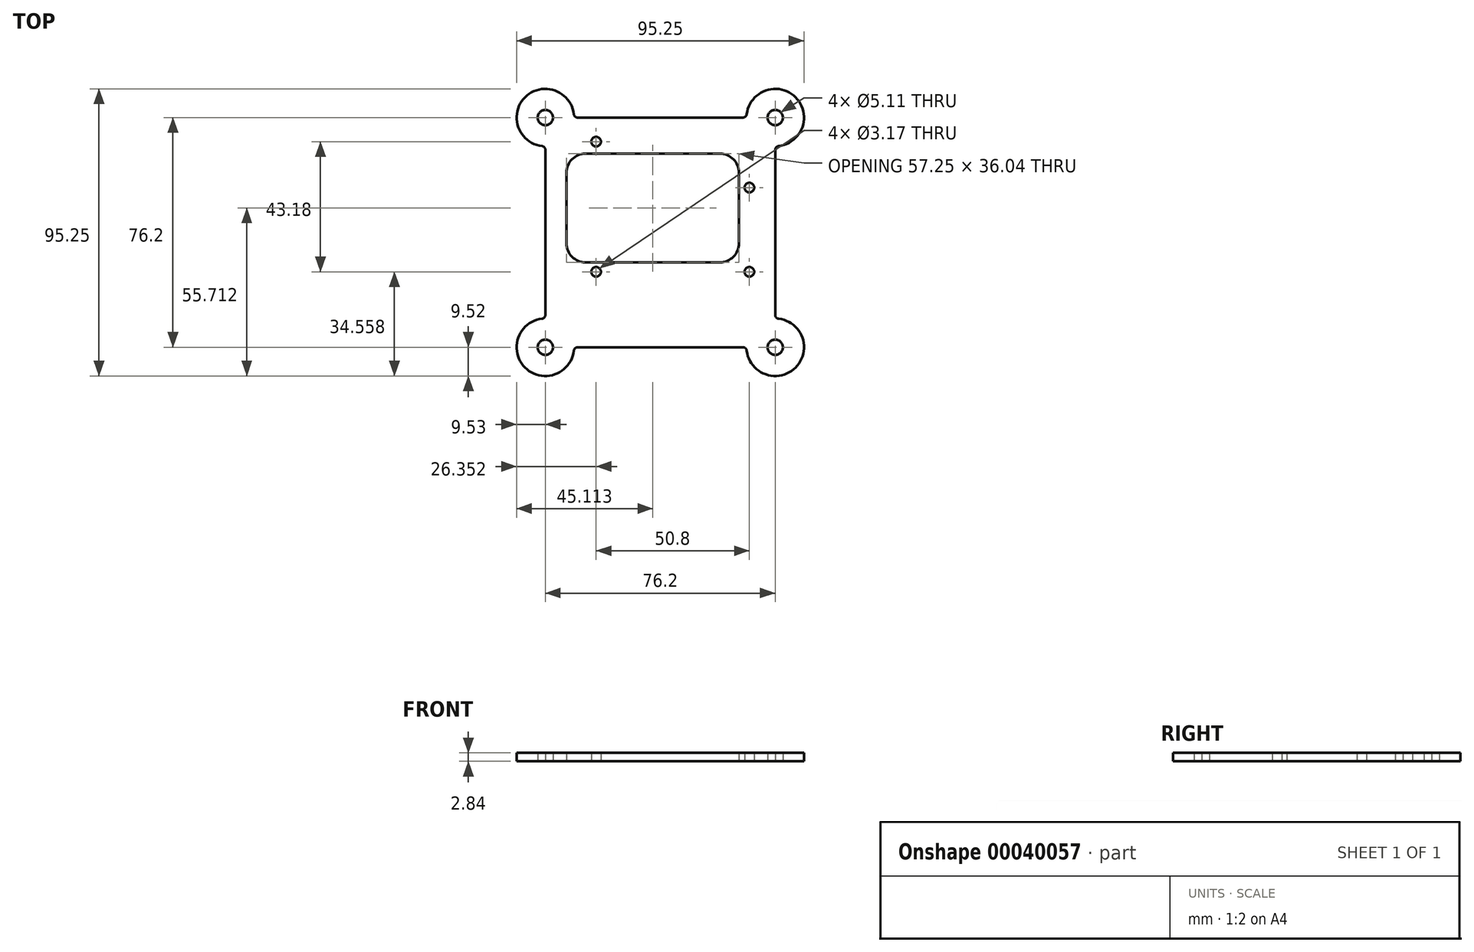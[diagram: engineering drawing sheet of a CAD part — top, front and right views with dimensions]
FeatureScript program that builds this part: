
annotation { "Feature Type Name" : "Feature", "Feature Type Description" : "" }
export const myFeature = defineFeature(function(context is Context, id is Id, definition is map)
    precondition{}
    {
        {
            var Q0;
            Q0=qCreatedBy(makeId("Top.planeOp"),FACE);
            var sketch = newSketch(context, id + "F0", { "sketchPlane" : qUnion([Q0])});
            skCircle(sketch, "E0", {"center": v(-21.62, 22.73) * mm, "radius": 1.59 * mm});
            skCircle(sketch, "E1", {"center": v(29.18, 7.49) * mm, "radius": 1.59 * mm});
            skCircle(sketch, "E2", {"center": v(29.18, -20.45) * mm, "radius": 1.59 * mm});
            skCircle(sketch, "E3", {"center": v(-21.62, -20.45) * mm, "radius": 1.59 * mm});
            skLineSegment(sketch, "E4.bottom", {"start": v(-27.72, 30.71) * mm, "end": v(27.04, 30.71) * mm});
            skLineSegment(sketch, "E4.top", {"start": v(-27.72, -45.49) * mm, "end": v(27.04, -45.49) * mm});
            skLineSegment(sketch, "E4.right", {"start": v(37.76, 20) * mm, "end": v(37.76, -34.77) * mm});
            skArc(sketch, "E5", {"start": v(38.88, 21.25) * mm, "mid": v(44.5, 37.45) * mm, "end": v(28.3, 31.83) * mm});
            skArc(sketch, "E6", {"start": v(28.3, -46.61) * mm, "mid": v(44.5, -52.22) * mm, "end": v(38.88, -36.03) * mm});
            skArc(sketch, "E7", {"start": v(-28.98, 31.83) * mm, "mid": v(-45.18, 37.45) * mm, "end": v(-39.56, 21.25) * mm});
            skArc(sketch, "E8", {"start": v(-39.56, -36.03) * mm, "mid": v(-45.18, -52.22) * mm, "end": v(-28.98, -46.61) * mm});
            skCircle(sketch, "E9", {"center": v(37.76, 30.71) * mm, "radius": 2.55 * mm});
            skCircle(sketch, "E10", {"center": v(-38.44, 30.71) * mm, "radius": 2.55 * mm});
            skCircle(sketch, "E11", {"center": v(-38.44, -45.49) * mm, "radius": 2.55 * mm});
            skCircle(sketch, "E12", {"center": v(37.76, -45.49) * mm, "radius": 2.55 * mm});
            skLineSegment(sketch, "E13.trimOffspring", {"start": v(-38.44, 20) * mm, "end": v(-38.44, -34.77) * mm});
            skLineSegment(sketch, "E14.bottom", {"start": v(-25.13, 18.72) * mm, "end": v(19.42, 18.72) * mm});
            skLineSegment(sketch, "E14.top", {"start": v(-25.13, -17.32) * mm, "end": v(19.42, -17.32) * mm});
            skLineSegment(sketch, "E14.left", {"start": v(-31.48, 12.37) * mm, "end": v(-31.48, -10.97) * mm});
            skLineSegment(sketch, "E14.right", {"start": v(25.77, 12.37) * mm, "end": v(25.77, -10.97) * mm});
            skPoint(sketch, "E15.visualSharp", {"position": v(-31.48, 18.72) * mm});
            skArc(sketch, "E15.filletArc", {"start": v(-25.13, 18.72) * mm, "mid": v(-29.62, 16.86) * mm, "end": v(-31.48, 12.37) * mm});
            skPoint(sketch, "E16.visualSharp", {"position": v(-31.48, -17.32) * mm});
            skArc(sketch, "E16.filletArc", {"start": v(-31.48, -10.97) * mm, "mid": v(-29.62, -15.46) * mm, "end": v(-25.13, -17.32) * mm});
            skPoint(sketch, "E17.visualSharp", {"position": v(25.77, -17.32) * mm});
            skArc(sketch, "E17.filletArc", {"start": v(19.42, -17.32) * mm, "mid": v(23.9, -15.46) * mm, "end": v(25.77, -10.97) * mm});
            skPoint(sketch, "E18.visualSharp", {"position": v(25.77, 18.72) * mm});
            skArc(sketch, "E18.filletArc", {"start": v(25.77, 12.37) * mm, "mid": v(23.9, 16.86) * mm, "end": v(19.42, 18.72) * mm});
            skArc(sketch, "E19", {"start": v(-28.98, 31.83) * mm, "mid": v(-28.56, 31.03) * mm, "end": v(-27.72, 30.71) * mm});
            skArc(sketch, "E20", {"start": v(27.04, 30.71) * mm, "mid": v(27.88, 31.03) * mm, "end": v(28.3, 31.83) * mm});
            skArc(sketch, "E21", {"start": v(-38.44, 20) * mm, "mid": v(-38.76, 20.83) * mm, "end": v(-39.56, 21.25) * mm});
            skArc(sketch, "E22", {"start": v(38.88, 21.25) * mm, "mid": v(38.08, 20.83) * mm, "end": v(37.76, 20) * mm});
            skArc(sketch, "E23", {"start": v(37.76, -34.77) * mm, "mid": v(38.08, -35.61) * mm, "end": v(38.88, -36.03) * mm});
            skArc(sketch, "E24", {"start": v(28.3, -46.61) * mm, "mid": v(27.88, -45.81) * mm, "end": v(27.04, -45.49) * mm});
            skArc(sketch, "E25", {"start": v(-27.72, -45.49) * mm, "mid": v(-28.56, -45.81) * mm, "end": v(-28.98, -46.61) * mm});
            skArc(sketch, "E26", {"start": v(-39.56, -36.03) * mm, "mid": v(-38.76, -35.61) * mm, "end": v(-38.44, -34.77) * mm});
            skSolve(sketch);
        }
        {
            var Q0;
            Q0=makeQuery(id+"F0.imprint","IMPRINT",FACE,{"disambiguationData":[TD([[makeQuery(id+"F0.imprint","IMPRINT",EDGE,{"derivedFrom":sQuery(id+"F0.wireOp",EDGE,"E0")}),-1.0]])]});
            extrude(context, id + "F1", {"entities" : qUnion([Q0]), "depth" : 2.84 * mm});
        }
    });
